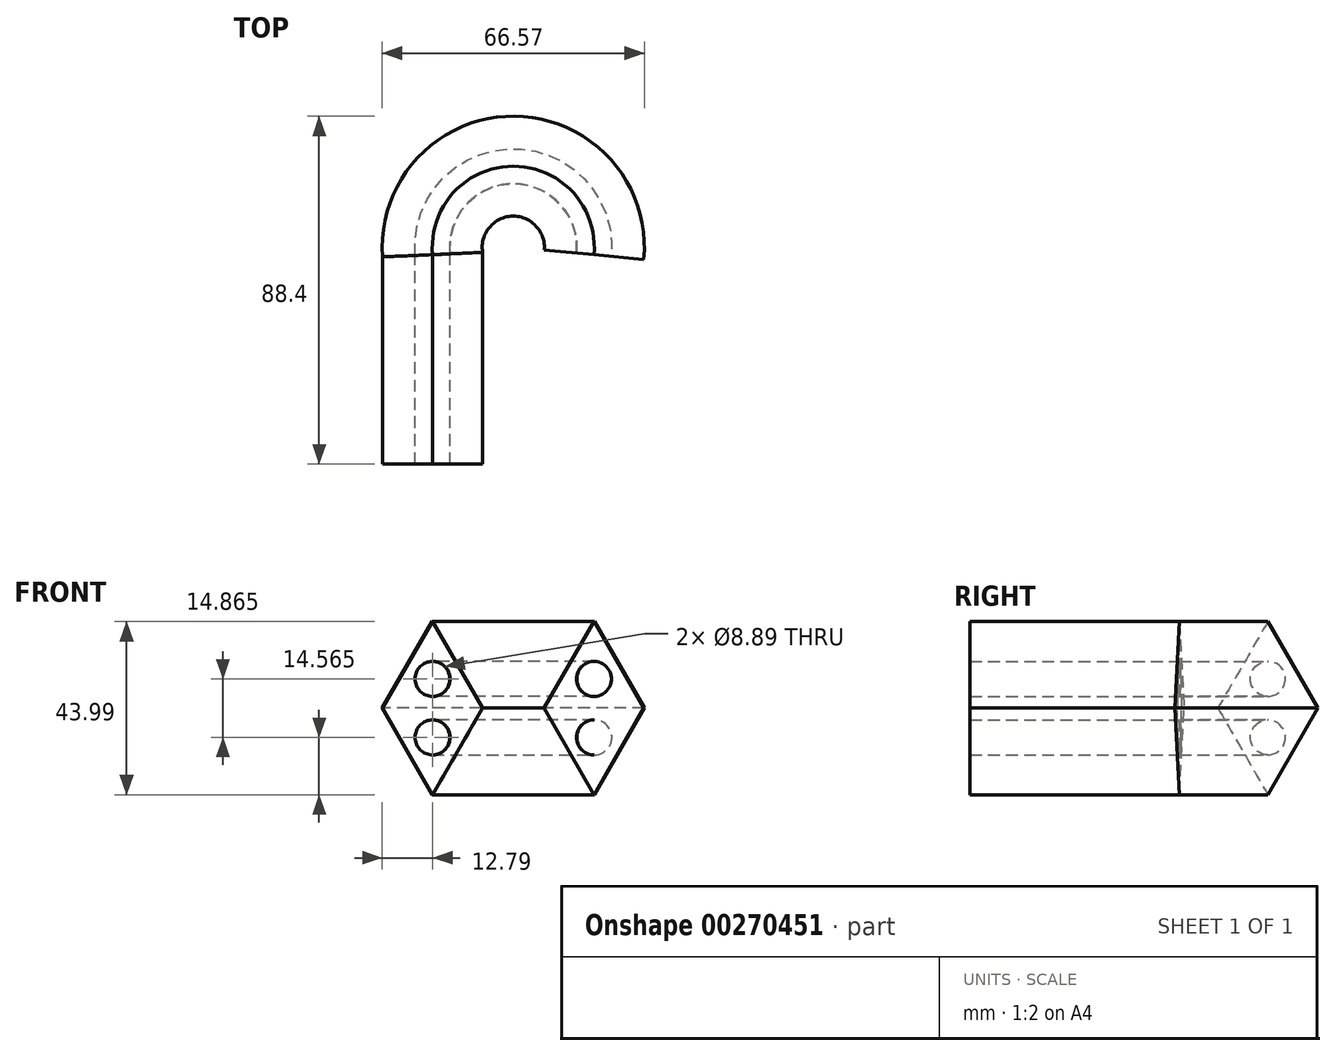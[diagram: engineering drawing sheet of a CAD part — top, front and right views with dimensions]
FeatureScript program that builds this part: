
annotation { "Feature Type Name" : "Feature", "Feature Type Description" : "" }
export const myFeature = defineFeature(function(context is Context, id is Id, definition is map)
    precondition{}
    {
        {
            var Q0;
            Q0=qCreatedBy(makeId("Top.planeOp"),FACE);
            var sketch = newSketch(context, id + "F0", { "sketchPlane" : qUnion([Q0])});
            skLineSegment(sketch, "E0", {"start": v(0, -30.55) * mm, "end": v(0, 22.66) * mm});
            skArc(sketch, "E1", {"start": v(41, 22.66) * mm, "mid": v(20.5, 45.15) * mm, "end": v(0, 22.66) * mm});
            skSolve(sketch);
        }
        {
            var Q0;
            Q0=qCreatedBy(makeId("Front.planeOp"),FACE);
            var sketch = newSketch(context, id + "F1", { "sketchPlane" : qUnion([Q0])});
            skLineSegment(sketch, "E2", {"start": v(0, 14.56) * mm, "end": v(12.7, -7.43) * mm});
            skLineSegment(sketch, "E3", {"start": v(12.7, -7.43) * mm, "end": v(-12.7, -7.43) * mm});
            skLineSegment(sketch, "E4", {"start": v(-12.7, -7.43) * mm, "end": v(0, 14.56) * mm});
            skCircle(sketch, "E5", {"center": v(0, 0) * mm, "radius": 4.44 * mm});
            skSolve(sketch);
        }
        {
            var Q0;
            Q0 = qSketchRegion(id + "F1", true);
            extrude(context, id + "F2", {"entities" : qUnion([Q0]), "depth" : 25.4 * mm});
        }
        {
            var Q0;
            Q0 = qSketchRegion(id + "F0", true);
            var Q1;
            Q1=makeQuery(id+"F2.opExtrude","CAP_FACE",FACE,{"disambiguationData":[OSD([sQuery(id+"F1.wireOp",EDGE,"E2"),sQuery(id+"F1.wireOp",EDGE,"E3"),sQuery(id+"F1.wireOp",EDGE,"E4")])],"isStart":false});
            var Q2;
            Q2=sQuery(id+"F0.wireOp",EDGE,"E1");
            var Q3;
            Q3=sQuery(id+"F0.wireOp",EDGE,"E0");
            sweep(context, id + "F3", {"operationType" : NewBodyOperationType.ADD, "profiles" : qUnion([Q0, Q1]), "path" : qUnion([Q2, Q3])});
        }
        {
            var Q0;
            Q0=makeQuery(id+"F2.opExtrude","SWEPT_BODY",BODY,{"disambiguationData":[OSD([sQuery(id+"F1.wireOp",EDGE,"E2"),sQuery(id+"F1.wireOp",EDGE,"E3"),sQuery(id+"F1.wireOp",EDGE,"E4")])]});
            var Q1;
            {var subQ0=sQuery(id+"F1.wireOp",EDGE,"E3");Q1=makeQuery(id+"F3.boolean.opBoolean","MERGE",FACE,{"derivedFrom":[makeQuery(id+"F2.opExtrude","SWEPT_FACE",FACE,{"disambiguationData":[OSD([subQ0])]}),makeQuery(id+"F3.opSweep","SWEPT_FACE",FACE,{"disambiguationData":[OSD([sQuery(id+"F0.wireOp",EDGE,"E0"),subQ0])]})]});}
            mirror(context, id + "F4", {"operationType" : NewBodyOperationType.ADD, "entities" : qUnion([Q0]), "mirrorPlane" : qUnion([Q1])});
        }
    });
